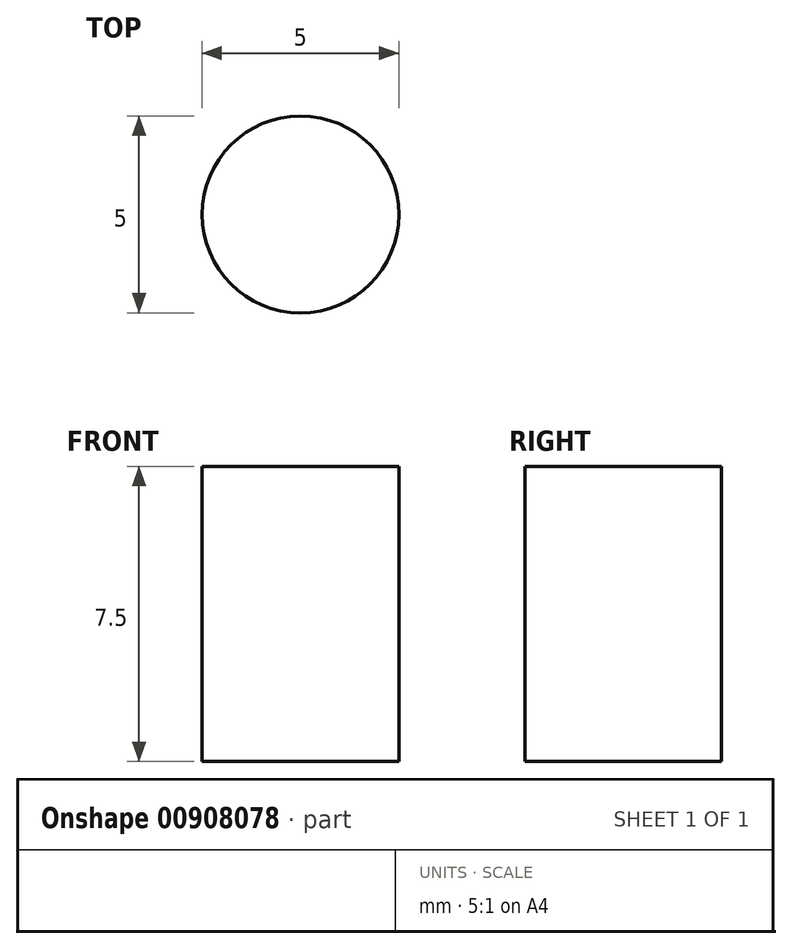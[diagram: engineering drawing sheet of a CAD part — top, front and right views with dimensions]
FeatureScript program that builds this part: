
annotation { "Feature Type Name" : "Feature", "Feature Type Description" : "" }
export const myFeature = defineFeature(function(context is Context, id is Id, definition is map)
    precondition{}
    {
        {
            var Q0;
            Q0=qCreatedBy(makeId("Top.planeOp"),FACE);
            var sketch = newSketch(context, id + "F0", { "sketchPlane" : qUnion([Q0])});
            skLineSegment(sketch, "E0", {"start": v(0, -6.67) * mm, "end": v(0, 6.86) * mm, "construction": true});
            skLineSegment(sketch, "E1", {"start": v(-7.08, 0) * mm, "end": v(6.13, 0) * mm, "construction": true});
            skCircle(sketch, "E2", {"center": v(0, 0) * mm, "radius": 2.5 * mm});
            skSolve(sketch);
        }
        {
            var Q0;
            Q0=makeQuery(id+"F0.imprint","IMPRINT",FACE,{"disambiguationData":[TD([[makeQuery(id+"F0.imprint","IMPRINT",EDGE,{"derivedFrom":sQuery(id+"F0.wireOp",EDGE,"E2")}),1.0]])]});
            extrude(context, id + "F1", {"entities" : qUnion([Q0]), "oppositeDirection" : true, "depth" : 7.5 * mm, "offsetDistance" : 25 * mm});
        }
    });
